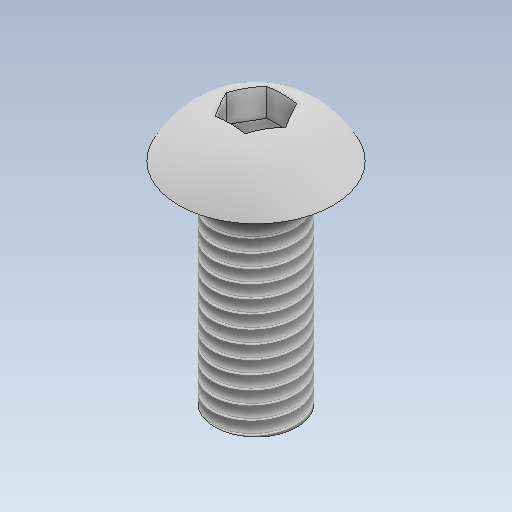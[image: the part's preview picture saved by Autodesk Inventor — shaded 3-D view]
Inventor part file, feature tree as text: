
AUTODESK INVENTOR PART (.ipt)
format: ipt  version: 2023 (Build 270158000, 158)  size: 154,112 bytes
history: native  units: in
note: dims shown in document units (in); Inventor stores cm internally (conversion verified against a paired STEP export)
features: other x3, sketch x3, plane x1
ambient origin geometry x8: Origin, YZ Plane, XZ Plane, XY Plane, X Axis, Y Axis, Z Axis, Center Point
bodies: Solid1 (feature_tree)
feature tree (7):
  other  "Screw.ipt"
  other  "Solid1::Screw.ipt"
  other  "TaggingFeature1"
  sketch  "Sketch1"  dims[d0=0.3937in]
  sketch  "Sketch2"
  sketch  "Sketch3"
  plane  "Work Plane1"
